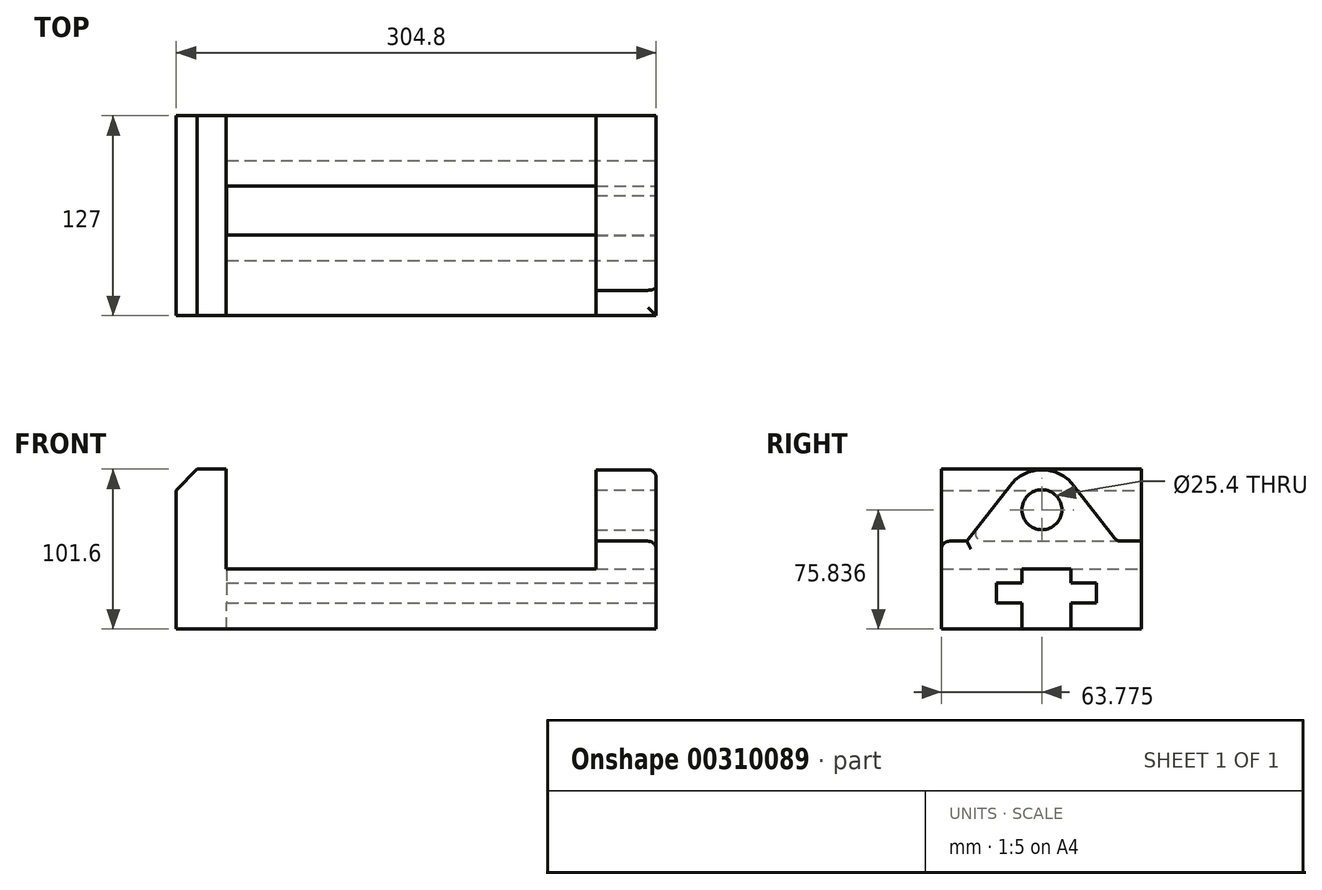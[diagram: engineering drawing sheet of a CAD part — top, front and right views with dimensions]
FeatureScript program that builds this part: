
annotation { "Feature Type Name" : "Feature", "Feature Type Description" : "" }
export const myFeature = defineFeature(function(context is Context, id is Id, definition is map)
    precondition{}
    {
        {
            var Q0;
            Q0=qCreatedBy(makeId("Front.planeOp"),FACE);
            var sketch = newSketch(context, id + "F0", { "sketchPlane" : qUnion([Q0])});
            skLineSegment(sketch, "E0", {"start": v(0, 0) * mm, "end": v(0, 87.99) * mm});
            skLineSegment(sketch, "E1", {"start": v(0, 87.99) * mm, "end": v(13.33, 101.6) * mm});
            skLineSegment(sketch, "E2", {"start": v(13.33, 101.6) * mm, "end": v(31.75, 101.6) * mm});
            skLineSegment(sketch, "E3", {"start": v(31.75, 101.6) * mm, "end": v(31.75, 38.1) * mm});
            skLineSegment(sketch, "E4", {"start": v(31.75, 38.1) * mm, "end": v(266.7, 38.1) * mm});
            skLineSegment(sketch, "E5", {"start": v(304.8, 0) * mm, "end": v(0, 0) * mm});
            skLineSegment(sketch, "E6", {"start": v(266.7, 55.88) * mm, "end": v(304.8, 55.88) * mm});
            skLineSegment(sketch, "E7", {"start": v(304.8, 0) * mm, "end": v(304.8, 55.88) * mm});
            skLineSegment(sketch, "E8", {"start": v(266.7, 55.88) * mm, "end": v(266.7, 38.1) * mm});
            skSolve(sketch);
        }
        {
            var Q0;
            Q0 = qSketchRegion(id + "F0", true);
            extrude(context, id + "F1", {"entities" : qUnion([Q0]), "depth" : 127 * mm});
        }
        {
            var Q0;
            Q0=makeQuery(id+"F1.opExtrude","SWEPT_FACE",FACE,{"disambiguationData":[OSD([sQuery(id+"F0.wireOp",EDGE,"E7")])]});
            var sketch = newSketch(context, id + "F2", { "sketchPlane" : qUnion([Q0])});
            skLineSegment(sketch, "E9", {"start": v(-110.85, 55.88) * mm, "end": v(-83.3, 91.4) * mm});
            skLineSegment(sketch, "E10", {"start": v(-15.6, 55.88) * mm, "end": v(-43.16, 91.4) * mm});
            skLineSegment(sketch, "E11", {"start": v(-15.6, 55.88) * mm, "end": v(-110.85, 55.88) * mm});
            skArc(sketch, "E12", {"start": v(-43.16, 91.4) * mm, "mid": v(-63.23, 101.24) * mm, "end": v(-83.3, 91.4) * mm});
            skSolve(sketch);
        }
        {
            var Q0;
            Q0 = qSketchRegion(id + "F2", true);
            extrude(context, id + "F3", {"entities" : qUnion([Q0]), "operationType" : NewBodyOperationType.ADD, "oppositeDirection" : true, "depth" : 38.35 * mm});
        }
        {
            var Q0;
            Q0=makeQuery(id+"F3.boolean.opBoolean","MERGE",FACE,{"derivedFrom":[makeQuery(id+"F1.opExtrude","SWEPT_FACE",FACE,{"disambiguationData":[OSD([sQuery(id+"F0.wireOp",EDGE,"E7")])]}),makeQuery(id+"F3.opExtrude","CAP_FACE",FACE,{"disambiguationData":[OSD([sQuery(id+"F2.wireOp",EDGE,"E9"),sQuery(id+"F2.wireOp",EDGE,"E10"),sQuery(id+"F2.wireOp",EDGE,"E11"),sQuery(id+"F2.wireOp",EDGE,"E12")])],"isStart":true})]});
            var sketch = newSketch(context, id + "F4", { "sketchPlane" : qUnion([Q0])});
            skCircle(sketch, "E13", {"center": v(-63.23, 75.84) * mm, "radius": 12.7 * mm});
            skSolve(sketch);
        }
        {
            var Q0;
            Q0 = qSketchRegion(id + "F4", true);
            extrude(context, id + "F5", {"entities" : qUnion([Q0]), "operationType" : NewBodyOperationType.REMOVE, "endBound" : BoundingType.SYMMETRIC, "oppositeDirection" : true, "depth" : 127 * mm});
        }
        {
            var Q0;
            Q0=makeQuery(id+"F3.boolean.opBoolean","MERGE",FACE,{"derivedFrom":[makeQuery(id+"F1.opExtrude","SWEPT_FACE",FACE,{"disambiguationData":[OSD([sQuery(id+"F0.wireOp",EDGE,"E7")])]}),makeQuery(id+"F3.opExtrude","CAP_FACE",FACE,{"disambiguationData":[OSD([sQuery(id+"F2.wireOp",EDGE,"E9"),sQuery(id+"F2.wireOp",EDGE,"E10"),sQuery(id+"F2.wireOp",EDGE,"E11"),sQuery(id+"F2.wireOp",EDGE,"E12")])],"isStart":true})]});
            var sketch = newSketch(context, id + "F6", { "sketchPlane" : qUnion([Q0])});
            skLineSegment(sketch, "E14", {"start": v(-75.84, 0) * mm, "end": v(-75.84, 16.51) * mm});
            skLineSegment(sketch, "E15", {"start": v(-75.84, 16.51) * mm, "end": v(-92, 16.51) * mm});
            skLineSegment(sketch, "E16", {"start": v(-92, 16.51) * mm, "end": v(-92, 29.21) * mm});
            skLineSegment(sketch, "E17", {"start": v(-92, 29.2) * mm, "end": v(-75.84, 29.21) * mm});
            skLineSegment(sketch, "E18", {"start": v(-75.84, 29.2) * mm, "end": v(-75.86, 38.1) * mm});
            skLineSegment(sketch, "E19", {"start": v(-75.86, 38.1) * mm, "end": v(-44.66, 38.15) * mm});
            skLineSegment(sketch, "E20", {"start": v(-44.66, 38.15) * mm, "end": v(-44.66, 29.21) * mm});
            skLineSegment(sketch, "E21", {"start": v(-44.66, 29.21) * mm, "end": v(-28.5, 29.21) * mm});
            skLineSegment(sketch, "E22", {"start": v(-28.5, 29.21) * mm, "end": v(-28.5, 16.51) * mm});
            skLineSegment(sketch, "E23", {"start": v(-28.5, 16.51) * mm, "end": v(-44.66, 16.51) * mm});
            skLineSegment(sketch, "E24", {"start": v(-44.66, 16.51) * mm, "end": v(-44.66, 0) * mm});
            skLineSegment(sketch, "E25", {"start": v(-44.66, 0) * mm, "end": v(-75.84, 0) * mm});
            skSolve(sketch);
        }
        {
            var Q0;
            Q0 = qSketchRegion(id + "F6", true);
            extrude(context, id + "F7", {"entities" : qUnion([Q0]), "operationType" : NewBodyOperationType.REMOVE, "oppositeDirection" : true, "depth" : 272.8 * mm});
        }
        {
            var Q0;
            Q0=makeQuery(id+"F3.opExtrude","CAP_EDGE",EDGE,{"disambiguationData":[OSD([sQuery(id+"F2.wireOp",EDGE,"E9")])],"isStart":true});
            var Q1;
            {var subQ0=sQuery(id+"F2.wireOp",EDGE,"E10");var subQ1=sQuery(id+"F0.wireOp",EDGE,"E7");var subQ2=sQuery(id+"F0.wireOp",EDGE,"E6");Q1=makeQuery(id+"F3.boolean.opBoolean","SPLIT",EDGE,{"disambiguationData":[TD([makeQuery(id+"F3.opExtrude","SWEPT_FACE",FACE,{"disambiguationData":[OSD([subQ0])]})])],"derivedFrom":makeQuery(id+"F1.opExtrude","SWEPT_EDGE",EDGE,{"disambiguationData":[OSD([subQ2,subQ1])]})});}
            var Q2;
            {var subQ0=sQuery(id+"F0.wireOp",EDGE,"E7");var subQ1=sQuery(id+"F2.wireOp",EDGE,"E9");var subQ2=sQuery(id+"F0.wireOp",EDGE,"E6");Q2=makeQuery(id+"F3.boolean.opBoolean","SPLIT",EDGE,{"disambiguationData":[TD([makeQuery(id+"F3.opExtrude","SWEPT_FACE",FACE,{"disambiguationData":[OSD([subQ1])]})])],"derivedFrom":makeQuery(id+"F1.opExtrude","SWEPT_EDGE",EDGE,{"disambiguationData":[OSD([subQ2,subQ0])]})});}
            var Q3;
            {var subQ0=sQuery(id+"F0.wireOp",EDGE,"E6");var subQ1=sQuery(id+"F2.wireOp",EDGE,"E9");Q3=makeQuery(id+"F3.boolean.opBoolean","SPLIT",EDGE,{"disambiguationData":[topologyDisambiguationEdgeConnected([makeQuery(id+"F1.opExtrude","SWEPT_FACE",FACE,{"disambiguationData":[OSD([subQ0])]})])],"derivedFrom":makeQuery(id+"F3.opExtrude","SWEPT_EDGE",EDGE,{"disambiguationData":[OSD([subQ0,sQuery(id+"F0.wireOp",EDGE,"E7"),subQ1,sQuery(id+"F2.wireOp",EDGE,"E11")])]})});}
            var Q4;
            Q4=makeQuery(id+"F1.opExtrude","CAP_EDGE",EDGE,{"disambiguationData":[OSD([sQuery(id+"F0.wireOp",EDGE,"E6")])],"isStart":false});
            var Q5;
            Q5=makeQuery(id+"F3.opExtrude","SWEPT_EDGE",EDGE,{"disambiguationData":[OSD([sQuery(id+"F2.wireOp",EDGE,"E9"),sQuery(id+"F2.wireOp",EDGE,"E12")])]});
            var Q6;
            {var subQ0=sQuery(id+"F0.wireOp",EDGE,"E6");var subQ1=sQuery(id+"F2.wireOp",EDGE,"E10");Q6=makeQuery(id+"F3.boolean.opBoolean","SPLIT",EDGE,{"disambiguationData":[topologyDisambiguationEdgeConnected([makeQuery(id+"F1.opExtrude","SWEPT_FACE",FACE,{"disambiguationData":[OSD([subQ0])]})])],"derivedFrom":makeQuery(id+"F3.opExtrude","SWEPT_EDGE",EDGE,{"disambiguationData":[OSD([subQ0,sQuery(id+"F0.wireOp",EDGE,"E7"),subQ1,sQuery(id+"F2.wireOp",EDGE,"E11")])]})});}
            var Q7;
            Q7=makeQuery(id+"F3.opExtrude","SWEPT_EDGE",EDGE,{"disambiguationData":[OSD([sQuery(id+"F2.wireOp",EDGE,"E10"),sQuery(id+"F2.wireOp",EDGE,"E12")])]});
            fillet(context, id + "F8", {"entities" : qUnion([Q0, Q1, Q2, Q3, Q4, Q5, Q6, Q7]), "radius" : 5.08 * mm, "tangentPropagation" : true, "allowEdgeOverflow" : false});
        }
    });
